# Revit family: КАМ
name_source: partatom
category: Оборудование
units: mm (PartAtom-declared; Revit-internal decimal feet)

## family parameters
Всегда вертикально = Да
Классификация = Нет
На основе рабочей плоскости = Нет
Общий = Нет
При загрузке вырезать с полостями = Нет
Размер круглого соединителя = Использовать диаметр
Тип детали = Нормальный
Точка принадлежности помещению = Нет

## types (7) — shared parameters
00_20_Виробник = Вентс
00_20_Назва = Камінний відцентровий вентилятор
P = 50 мм
URL = https://vents.ua
Изготовитель = Вентс
КФК = Да
Класифікація навантаження = HVAC
Кількість фаз = 1
Матеріал зони обслуговуваня = <По категории>
Матеріал корпусу = Сталь, гальванизированная
Напруга = 230 В
Частота = 50 Гц
zero-valued in all types: Отметка по умолчанию

## per-type parameters (varying)
- КАМ 125: B=245 мм; D=125 мм; Dy=115 мм; H=350 мм; H1=300 мм; Hn=250 мм; Hv=610 мм; L=260 мм; Lk=115 мм; b=123 мм; b2=113 мм; h1=83 мм; l=210 мм; l1=105 мм; l2=95 мм; Вага=8.50 кг; Вага КАМ=5.82 кг; Вага з КФК=8.50 кг; Висота=610 мм; Довжина=260 мм; Діаметр=125 мм; КФК_О=КФК : КФК 125; Максимальний потік повітря=400.0 м³/ч; Потужність=108 Вт; Рівень звукового тиску на відстані 3 м=42 дБА; Струм=1 А; Установлена потужність=186 В·А; Ширина=295 мм
- КАМ 160: B=285 мм; D=160 мм; Dy=150 мм; H=350 мм; H1=300 мм; Hn=250 мм; Hv=650 мм; L=300 мм; Lk=135 мм; b=143 мм; b2=133 мм; h1=100 мм; l=250 мм; l1=125 мм; l2=115 мм; Вага=9.70 кг; Вага КАМ=6.90 кг; Вага з КФК=9.70 кг; Висота=650 мм; Довжина=300 мм; Діаметр=160 мм; КФК_О=КФК : КФК 160; Максимальний потік повітря=540.0 м³/ч; Потужність=116 Вт; Рівень звукового тиску на відстані 3 м=42 дБА; Струм=1 А; Установлена потужність=198 В·А; Ширина=335 мм
- КАМ 150: B=285 мм; D=150 мм; Dy=140 мм; H=350 мм; H1=300 мм; Hn=250 мм; Hv=650 мм; L=300 мм; Lk=135 мм; b=143 мм; b2=133 мм; h1=95 мм; l=250 мм; l1=125 мм; l2=115 мм; Вага=9.70 кг; Вага КАМ=6.90 кг; Вага з КФК=9.70 кг; Висота=650 мм; Довжина=300 мм; Діаметр=150 мм; КФК_О=КФК : КФК150; Максимальний потік повітря=520.0 м³/ч; Потужність=115 Вт; Рівень звукового тиску на відстані 3 м=42 дБА; Струм=1 А; Установлена потужність=193 В·А; Ширина=335 мм
- КАМ 125 Еко: B=245 мм; D=125 мм; Dy=115 мм; H=320 мм; H1=270 мм; Hn=220 мм; Hv=550 мм; L=260 мм; Lk=115 мм; b=123 мм; b2=113 мм; h1=83 мм; l=210 мм; l1=105 мм; l2=95 мм; Вага=9.40 кг; Вага КАМ=5.82 кг; Вага з КФК=9.40 кг; Висота=550 мм; Довжина=260 мм; Діаметр=125 мм; КФК_О=КФК : КФК 125; Максимальний потік повітря=350.0 м³/ч; Потужність=32 Вт; Рівень звукового тиску на відстані 3 м=37 дБА; Струм=0 А; Установлена потужність=32 В·А; Ширина=295 мм
- КАМ 150 Еко: B=285 мм; D=150 мм; Dy=140 мм; H=320 мм; H1=270 мм; Hn=220 мм; Hv=590 мм; L=300 мм; Lk=135 мм; b=143 мм; b2=133 мм; h1=95 мм; l=250 мм; l1=125 мм; l2=115 мм; Вага=10.80 кг; Вага КАМ=6.90 кг; Вага з КФК=10.80 кг; Висота=590 мм; Довжина=300 мм; Діаметр=150 мм; КФК_О=КФК : КФК 150 Еко; Максимальний потік повітря=450.0 м³/ч; Потужність=43 Вт; Рівень звукового тиску на відстані 3 м=39 дБА; Струм=0 А; Установлена потужність=44 В·А; Ширина=335 мм
- КАМ 160 Еко: B=285 мм; D=160 мм; Dy=150 мм; H=320 мм; H1=270 мм; Hn=220 мм; Hv=590 мм; L=300 мм; Lk=135 мм; b=143 мм; b2=133 мм; h1=100 мм; l=250 мм; l1=125 мм; l2=115 мм; Вага=10.80 кг; Вага КАМ=6.90 кг; Вага з КФК=10.80 кг; Висота=590 мм; Довжина=300 мм; Діаметр=160 мм; КФК_О=КФК : КФК 160 Еко; Максимальний потік повітря=470.0 м³/ч; Потужність=44 Вт; Рівень звукового тиску на відстані 3 м=39 дБА; Струм=0 А; Установлена потужність=44 В·А; Ширина=335 мм
- КАМ 150 Еко макс: B=285 мм; D=150 мм; Dy=140 мм; H=320 мм; H1=270 мм; Hn=220 мм; Hv=590 мм; L=300 мм; Lk=135 мм; b=143 мм; b2=133 мм; h1=95 мм; l=250 мм; l1=125 мм; l2=115 мм; Вага=10.80 кг; Вага КАМ=6.90 кг; Вага з КФК=10.80 кг; Висота=590 мм; Довжина=300 мм; Діаметр=150 мм; КФК_О=КФК : КФК 150 Еко макс; Максимальний потік повітря=613.0 м³/ч; Потужність=115 Вт; Рівень звукового тиску на відстані 3 м=45 дБА; Струм=1 А; Установлена потужність=117 В·А; Ширина=335 мм

note: column(s) folded — value = type name in every type: 00_20_Тип
